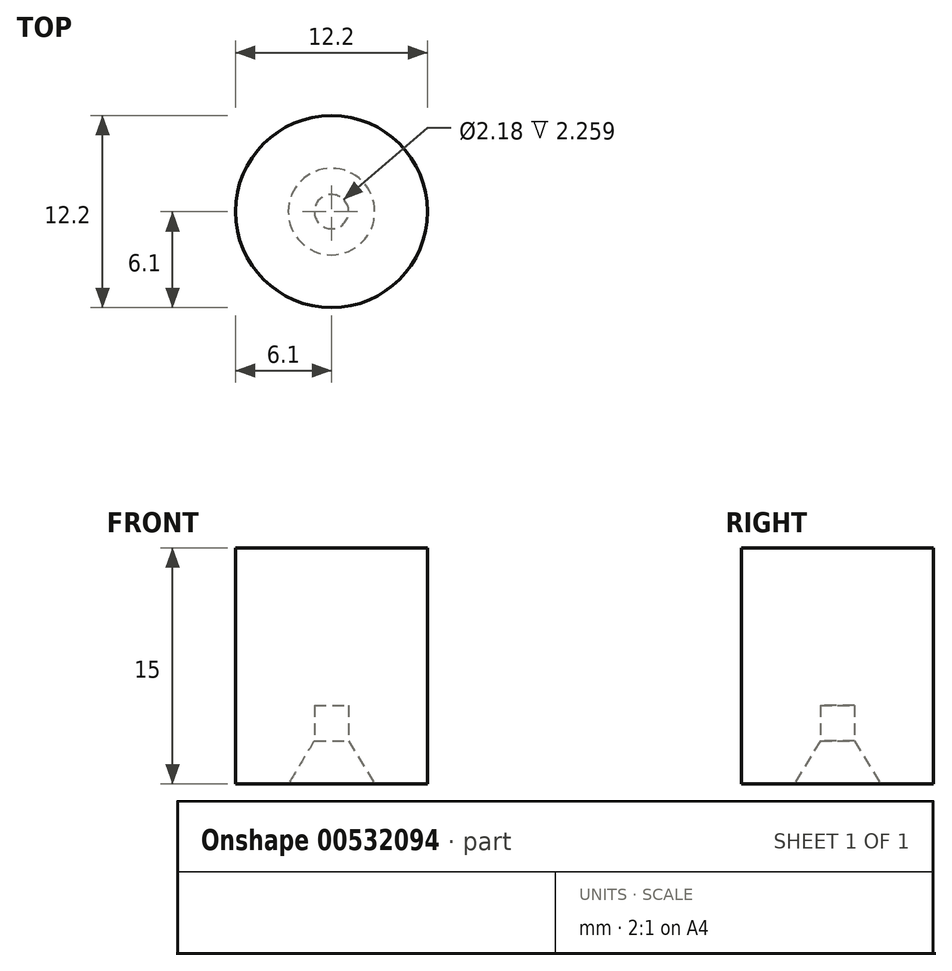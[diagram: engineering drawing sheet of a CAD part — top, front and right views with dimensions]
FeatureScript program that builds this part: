
annotation { "Feature Type Name" : "Feature", "Feature Type Description" : "" }
export const myFeature = defineFeature(function(context is Context, id is Id, definition is map)
    precondition{}
    {
        {
            var Q0;
            Q0=qCreatedBy(makeId("Top.planeOp"),FACE);
            var sketch = newSketch(context, id + "F0", { "sketchPlane" : qUnion([Q0])});
            skCircle(sketch, "E0", {"center": v(0, 0) * mm, "radius": 6.1 * mm});
            skSolve(sketch);
        }
        {
            var Q0;
            Q0 = qSketchRegion(id + "F0", true);
            extrude(context, id + "F1", {"entities" : qUnion([Q0]), "depth" : 15 * mm, "offsetDistance" : 25 * mm});
        }
        {
            var Q0;
            Q0=qCreatedBy(makeId("Front.planeOp"),FACE);
            var sketch = newSketch(context, id + "F2", { "sketchPlane" : qUnion([Q0])});
            skLineSegment(sketch, "E1", {"start": v(0, 0) * mm, "end": v(1.19, 0) * mm});
            skLineSegment(sketch, "E2", {"start": v(1.19, 0) * mm, "end": v(0, 4.54) * mm});
            skLineSegment(sketch, "E3", {"start": v(0, 4.54) * mm, "end": v(0, 0) * mm});
            skLineSegment(sketch, "E4", {"start": v(0, 4.54) * mm, "end": v(2.75, 0) * mm});
            skLineSegment(sketch, "E5", {"start": v(2.75, 0) * mm, "end": v(0, 0) * mm});
            skSolve(sketch);
        }
        {
            var Q0;
            Q0 = qSketchRegion(id + "F2", true);
            var Q1;
            Q1=sQuery(id+"F2.wireOp",EDGE,"E3");
            revolve(context, id + "F3", {"operationType" : NewBodyOperationType.REMOVE, "entities" : qUnion([Q0]), "axis" : qUnion([Q1]), "revolveType" : RevolveType.FULL, "oppositeDirection" : true});
        }
        {
            var Q0;
            Q0=makeQuery(id+"F1.opExtrude","CAP_FACE",FACE,{"disambiguationData":[OSD([sQuery(id+"F0.wireOp",EDGE,"E0")])],"isStart":true});
            var sketch = newSketch(context, id + "F4", { "sketchPlane" : qUnion([Q0])});
            skCircle(sketch, "E6", {"center": v(0, 0) * mm, "radius": 1.09 * mm});
            skSolve(sketch);
        }
        {
            var Q0;
            Q0 = qSketchRegion(id + "F4", true);
            extrude(context, id + "F5", {"entities" : qUnion([Q0]), "operationType" : NewBodyOperationType.REMOVE, "oppositeDirection" : true, "depth" : 5 * mm, "offsetDistance" : 25 * mm});
        }
    });
